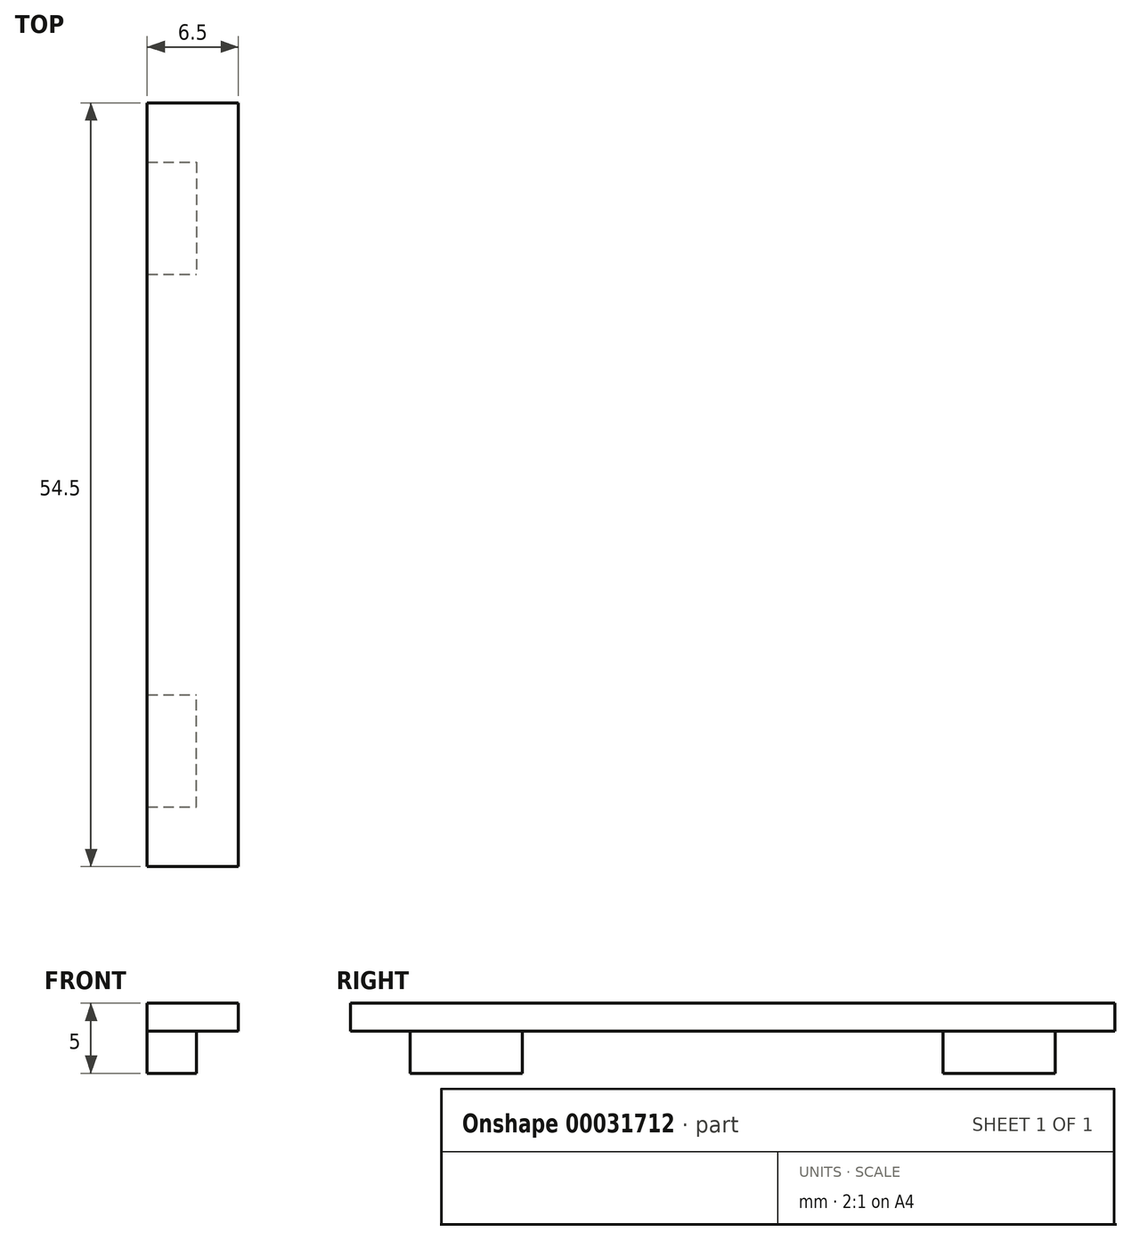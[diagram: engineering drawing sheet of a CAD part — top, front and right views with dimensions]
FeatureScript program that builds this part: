
annotation { "Feature Type Name" : "Feature", "Feature Type Description" : "" }
export const myFeature = defineFeature(function(context is Context, id is Id, definition is map)
    precondition{}
    {
        {
            var Q0;
            Q0=qCreatedBy(makeId("Top.planeOp"),FACE);
            var sketch = newSketch(context, id + "F0", { "sketchPlane" : qUnion([Q0])});
            skLineSegment(sketch, "E0.bottom", {"start": v(0, 0) * mm, "end": v(6.5, 0) * mm});
            skLineSegment(sketch, "E0.top", {"start": v(0, 54.5) * mm, "end": v(6.5, 54.5) * mm});
            skLineSegment(sketch, "E0.left", {"start": v(0, 0) * mm, "end": v(0, 54.5) * mm});
            skLineSegment(sketch, "E0.right", {"start": v(6.5, 0) * mm, "end": v(6.5, 54.5) * mm});
            skSolve(sketch);
        }
        {
            var Q0;
            Q0 = qSketchRegion(id + "F0", true);
            extrude(context, id + "F1", {"entities" : qUnion([Q0]), "depth" : 2 * mm});
        }
        {
            var Q0;
            Q0=makeQuery(id+"F1.opExtrude","CAP_FACE",FACE,{"disambiguationData":[OSD([sQuery(id+"F0.wireOp",EDGE,"E0.bottom"),sQuery(id+"F0.wireOp",EDGE,"E0.top"),sQuery(id+"F0.wireOp",EDGE,"E0.left"),sQuery(id+"F0.wireOp",EDGE,"E0.right")])],"isStart":true});
            var sketch = newSketch(context, id + "F2", { "sketchPlane" : qUnion([Q0])});
            skLineSegment(sketch, "E1", {"start": v(-22.67, -27.25) * mm, "end": v(42.57, -27.25) * mm, "construction": true});
            skLineSegment(sketch, "E2.bottom", {"start": v(0, -50.25) * mm, "end": v(3.5, -50.25) * mm});
            skLineSegment(sketch, "E2.top", {"start": v(0, -42.25) * mm, "end": v(3.5, -42.25) * mm});
            skLineSegment(sketch, "E2.left", {"start": v(0, -50.25) * mm, "end": v(0, -42.25) * mm});
            skLineSegment(sketch, "E2.right", {"start": v(3.5, -50.25) * mm, "end": v(3.5, -42.25) * mm});
            skLineSegment(sketch, "E3.MirrorCS", {"start": v(3.5, -4.25) * mm, "end": v(3.5, -12.25) * mm});
            skLineSegment(sketch, "E4.MirrorCS", {"start": v(0, -4.25) * mm, "end": v(0, -12.25) * mm});
            skLineSegment(sketch, "E5.MirrorCS", {"start": v(0, -12.25) * mm, "end": v(3.5, -12.25) * mm});
            skLineSegment(sketch, "E6.MirrorCS", {"start": v(0, -4.25) * mm, "end": v(3.5, -4.25) * mm});
            skSolve(sketch);
        }
        {
            var Q0;
            Q0 = qSketchRegion(id + "F2", true);
            extrude(context, id + "F3", {"entities" : qUnion([Q0]), "operationType" : NewBodyOperationType.ADD, "depth" : 3 * mm});
        }
    });
